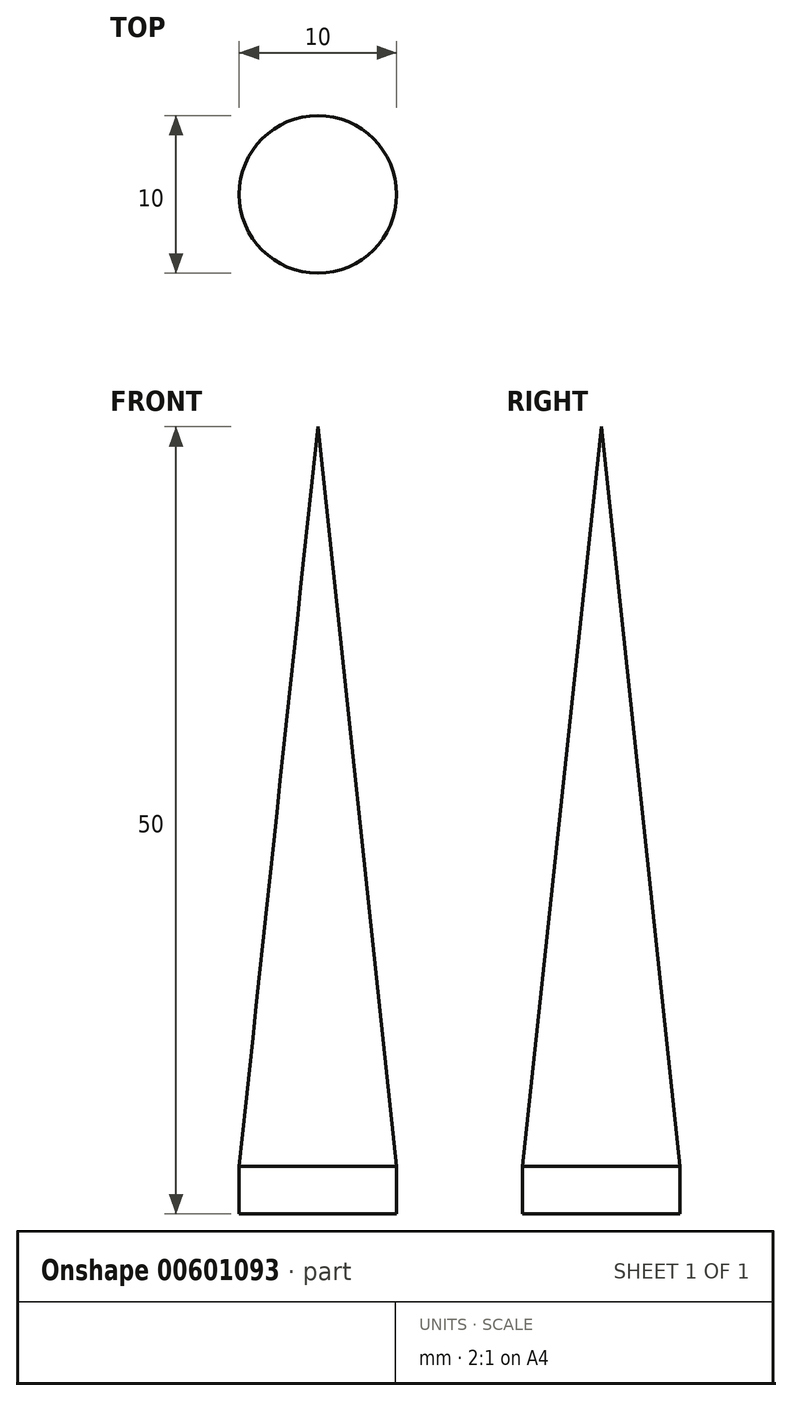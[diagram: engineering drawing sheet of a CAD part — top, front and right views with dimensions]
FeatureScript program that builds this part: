
annotation { "Feature Type Name" : "Feature", "Feature Type Description" : "" }
export const myFeature = defineFeature(function(context is Context, id is Id, definition is map)
    precondition{}
    {
        {
            var Q0;
            Q0=qCreatedBy(makeId("Front.planeOp"),FACE);
            var sketch = newSketch(context, id + "F0", { "sketchPlane" : qUnion([Q0])});
            skLineSegment(sketch, "E0", {"start": v(5, -19.58) * mm, "end": v(0, 27.42) * mm});
            skLineSegment(sketch, "E1", {"start": v(5, -22.58) * mm, "end": v(5, -19.58) * mm});
            skLineSegment(sketch, "E2", {"start": v(5, -22.58) * mm, "end": v(0, -22.58) * mm});
            skLineSegment(sketch, "E3", {"start": v(0, -22.58) * mm, "end": v(0, 27.42) * mm});
            skSolve(sketch);
        }
        {
            var Q0;
            Q0=makeQuery(id+"F0.imprint","IMPRINT",FACE,{"disambiguationData":[TD([[makeQuery(id+"F0.imprint","IMPRINT",EDGE,{"derivedFrom":sQuery(id+"F0.wireOp",EDGE,"E0")}),1.0]])]});
            var Q1;
            Q1=sQuery(id+"F0.wireOp",EDGE,"E3");
            revolve(context, id + "F1", {"entities" : qUnion([Q0]), "axis" : qUnion([Q1]), "revolveType" : RevolveType.FULL});
        }
        {
            var Q0;
            Q0=qCreatedBy(makeId("Front.planeOp"),FACE);
            var sketch = newSketch(context, id + "F2", { "sketchPlane" : qUnion([Q0])});
            skCircle(sketch, "E4", {"center": v(-18.55, 8.47) * mm, "radius": 3.18 * mm});
            skCircle(sketch, "E5", {"center": v(-18.55, 8.47) * mm, "radius": 1.53 * mm});
            skLineSegment(sketch, "E6", {"start": v(0, 21.3) * mm, "end": v(0, 5.24) * mm});
            skLineSegment(sketch, "E7", {"start": v(3.87, 21.3) * mm, "end": v(7, 21.3) * mm});
            skLineSegment(sketch, "E8", {"start": v(7, 21.3) * mm, "end": v(3.97, 13.36) * mm});
            skLineSegment(sketch, "E9", {"start": v(3.97, 13.36) * mm, "end": v(7, 5.24) * mm});
            skLineSegment(sketch, "E10", {"start": v(7, 5.24) * mm, "end": v(3.97, 5.24) * mm});
            skLineSegment(sketch, "E11", {"start": v(3.87, 21.3) * mm, "end": v(2.54, 13.37) * mm});
            skLineSegment(sketch, "E12", {"start": v(2.54, 13.37) * mm, "end": v(3.97, 5.24) * mm});
            skSolve(sketch);
        }
        {
            var Q0;
            Q0=sQuery(id+"F2.wireOp",EDGE,"E7");
            var Q1;
            Q1=sQuery(id+"F2.wireOp",EDGE,"E8");
            var Q2;
            Q2=sQuery(id+"F2.wireOp",EDGE,"E9");
            var Q3;
            Q3=sQuery(id+"F2.wireOp",EDGE,"E10");
            var Q4;
            Q4=sQuery(id+"F2.wireOp",EDGE,"E11");
            var Q5;
            Q5=sQuery(id+"F2.wireOp",EDGE,"E12");
            var Q6;
            Q6=sQuery(id+"F2.wireOp",EDGE,"E6");
            revolve(context, id + "F3", {"bodyType" : ToolBodyType.SURFACE, "surfaceEntities" : qUnion([Q0, Q1, Q2, Q3, Q4, Q5]), "axis" : qUnion([Q6]), "revolveType" : RevolveType.FULL});
        }
        {
            var Q0;
            Q0=makeQuery(id+"F3.opRevolve","SWEPT_EDGE",EDGE,{"disambiguationData":[OSD([sQuery(id+"F2.wireOp",VERTEX,"E9.start")])]});
            fillet(context, id + "F4", {"entities" : qUnion([Q0]), "radius" : 7.24 * mm, "tangentPropagation" : true, "allowEdgeOverflow" : false});
        }
        {
            var Q0;
            Q0=makeQuery(id+"F3.opRevolve","SWEPT_EDGE",EDGE,{"disambiguationData":[OSD([sQuery(id+"F2.wireOp",VERTEX,"E8.start")])]});
            fillet(context, id + "F5", {"entities" : qUnion([Q0]), "radius" : 2 * mm, "tangentPropagation" : true, "allowEdgeOverflow" : false});
        }
        {
            var Q0;
            Q0=makeQuery(id+"F3.opRevolve","SWEPT_EDGE",EDGE,{"disambiguationData":[OSD([sQuery(id+"F2.wireOp",VERTEX,"E10.start")])]});
            fillet(context, id + "F6", {"entities" : qUnion([Q0]), "radius" : 2 * mm, "tangentPropagation" : true, "allowEdgeOverflow" : false});
        }
    });
